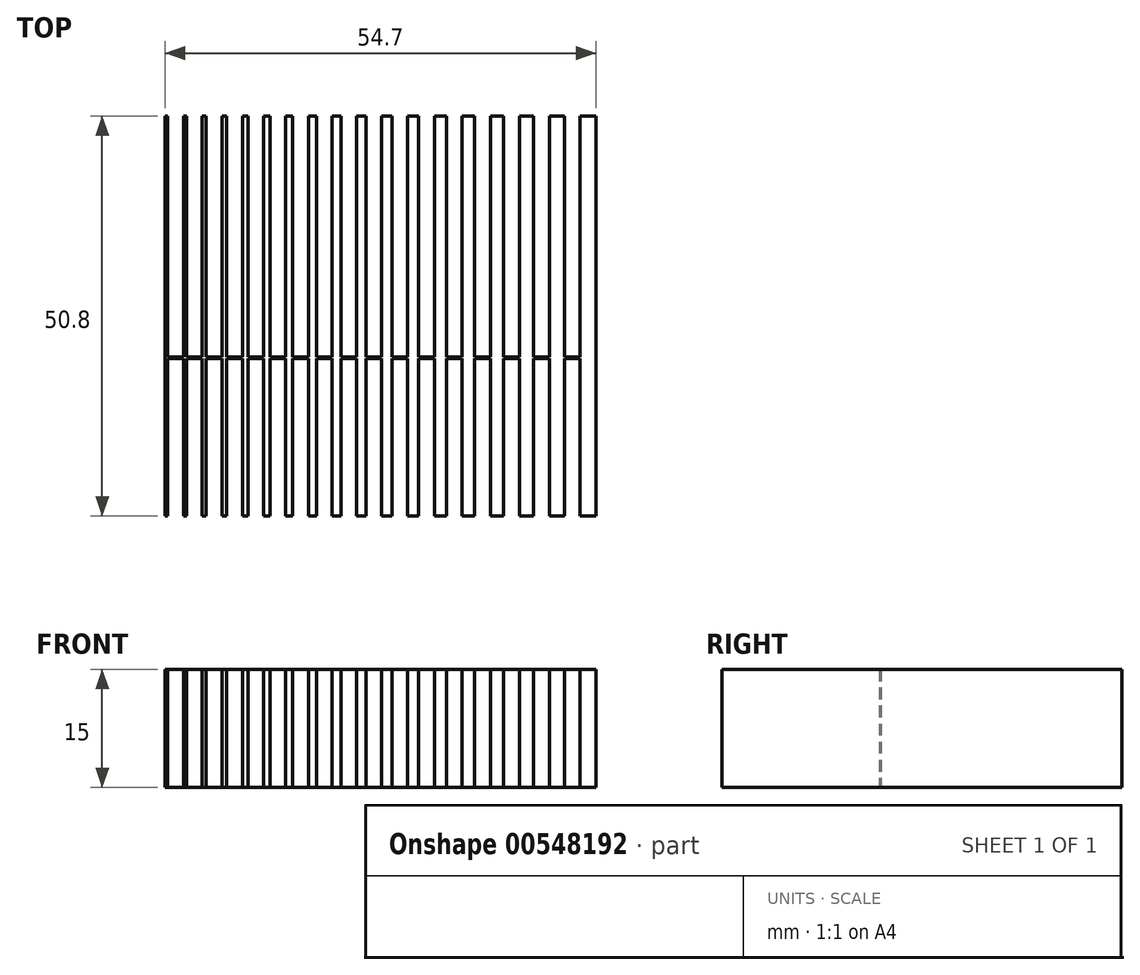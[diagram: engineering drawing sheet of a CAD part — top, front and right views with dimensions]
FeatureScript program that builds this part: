
annotation { "Feature Type Name" : "Feature", "Feature Type Description" : "" }
export const myFeature = defineFeature(function(context is Context, id is Id, definition is map)
    precondition{}
    {
        {
            var Q0;
            Q0=qCreatedBy(makeId("Top.planeOp"),FACE);
            var sketch = newSketch(context, id + "F0", { "sketchPlane" : qUnion([Q0])});
            skLineSegment(sketch, "E0.bottom", {"start": v(-25.4, 25.4) * mm, "end": v(34.6, 25.4) * mm, "construction": true});
            skLineSegment(sketch, "E0.top", {"start": v(-25.4, -25.4) * mm, "end": v(34.6, -25.4) * mm, "construction": true});
            skLineSegment(sketch, "E0.left", {"start": v(-25.4, 25.4) * mm, "end": v(-25.4, -25.4) * mm, "construction": true});
            skLineSegment(sketch, "E0.right", {"start": v(34.6, 25.4) * mm, "end": v(34.6, -25.4) * mm, "construction": true});
            skLineSegment(sketch, "E1.bottom", {"start": v(-23.4, 25.4) * mm, "end": v(-23.1, 25.4) * mm});
            skLineSegment(sketch, "E1.top", {"start": v(-23.4, -25.4) * mm, "end": v(-23.1, -25.4) * mm});
            skLineSegment(sketch, "E1.left", {"start": v(-23.4, 25.4) * mm, "end": v(-23.4, -25.4) * mm});
            skLineSegment(sketch, "E1.right", {"start": v(-23.1, 25.4) * mm, "end": v(-23.1, -5.2) * mm});
            skLineSegment(sketch, "E2.bottom", {"start": v(-21.1, 25.4) * mm, "end": v(-20.7, 25.4) * mm});
            skLineSegment(sketch, "E2.top", {"start": v(-21.1, -25.4) * mm, "end": v(-20.7, -25.4) * mm});
            skLineSegment(sketch, "E2.left", {"start": v(-21.1, 25.4) * mm, "end": v(-21.1, -5.2) * mm});
            skLineSegment(sketch, "E2.right", {"start": v(-20.7, 25.4) * mm, "end": v(-20.7, -5.2) * mm});
            skLineSegment(sketch, "E3.bottom", {"start": v(-18.7, 25.4) * mm, "end": v(-18.2, 25.4) * mm});
            skLineSegment(sketch, "E3.top", {"start": v(-18.7, -25.4) * mm, "end": v(-18.2, -25.4) * mm});
            skLineSegment(sketch, "E3.left", {"start": v(-18.7, 25.4) * mm, "end": v(-18.7, -5.2) * mm});
            skLineSegment(sketch, "E3.right", {"start": v(-18.2, 25.4) * mm, "end": v(-18.2, -5.2) * mm});
            skLineSegment(sketch, "E4.bottom", {"start": v(-16.2, 25.4) * mm, "end": v(-15.6, 25.4) * mm});
            skLineSegment(sketch, "E4.top", {"start": v(-16.2, -25.4) * mm, "end": v(-15.6, -25.4) * mm});
            skLineSegment(sketch, "E4.left", {"start": v(-16.2, 25.4) * mm, "end": v(-16.2, -5.2) * mm});
            skLineSegment(sketch, "E4.right", {"start": v(-15.6, 25.4) * mm, "end": v(-15.6, -5.2) * mm});
            skLineSegment(sketch, "E5.bottom", {"start": v(-13.6, 25.4) * mm, "end": v(-12.9, 25.4) * mm});
            skLineSegment(sketch, "E5.top", {"start": v(-13.6, -25.4) * mm, "end": v(-12.9, -25.4) * mm});
            skLineSegment(sketch, "E5.left", {"start": v(-13.6, 25.4) * mm, "end": v(-13.6, -5.2) * mm});
            skLineSegment(sketch, "E5.right", {"start": v(-12.9, 25.4) * mm, "end": v(-12.9, -5.2) * mm});
            skLineSegment(sketch, "E6.bottom", {"start": v(-10.9, 25.4) * mm, "end": v(-10.1, 25.4) * mm});
            skLineSegment(sketch, "E6.top", {"start": v(-10.9, -25.4) * mm, "end": v(-10.1, -25.4) * mm});
            skLineSegment(sketch, "E6.left", {"start": v(-10.9, 25.4) * mm, "end": v(-10.9, -5.2) * mm});
            skLineSegment(sketch, "E6.right", {"start": v(-10.1, 25.4) * mm, "end": v(-10.1, -5.2) * mm});
            skLineSegment(sketch, "E7.bottom", {"start": v(-8.1, 25.4) * mm, "end": v(-7.2, 25.4) * mm});
            skLineSegment(sketch, "E7.top", {"start": v(-8.1, -25.4) * mm, "end": v(-7.2, -25.4) * mm});
            skLineSegment(sketch, "E7.left", {"start": v(-8.1, 25.4) * mm, "end": v(-8.1, -5.2) * mm});
            skLineSegment(sketch, "E7.right", {"start": v(-7.2, 25.4) * mm, "end": v(-7.2, -5.2) * mm});
            skLineSegment(sketch, "E8.bottom", {"start": v(-5.2, 25.4) * mm, "end": v(-4.2, 25.4) * mm});
            skLineSegment(sketch, "E8.top", {"start": v(-5.2, -25.4) * mm, "end": v(-4.2, -25.4) * mm});
            skLineSegment(sketch, "E8.left", {"start": v(-5.2, 25.4) * mm, "end": v(-5.2, -5.2) * mm});
            skLineSegment(sketch, "E8.right", {"start": v(-4.2, 25.4) * mm, "end": v(-4.2, -5.2) * mm});
            skLineSegment(sketch, "E9.bottom", {"start": v(-2.2, 25.4) * mm, "end": v(-1.1, 25.4) * mm});
            skLineSegment(sketch, "E9.top", {"start": v(-2.2, -25.4) * mm, "end": v(-1.1, -25.4) * mm});
            skLineSegment(sketch, "E9.left", {"start": v(-2.2, 25.4) * mm, "end": v(-2.2, -5.2) * mm});
            skLineSegment(sketch, "E9.right", {"start": v(-1.1, 25.4) * mm, "end": v(-1.1, -5.2) * mm});
            skLineSegment(sketch, "E10.bottom", {"start": v(0.9, 25.4) * mm, "end": v(2.1, 25.4) * mm});
            skLineSegment(sketch, "E10.top", {"start": v(0.9, -25.4) * mm, "end": v(2.1, -25.4) * mm});
            skLineSegment(sketch, "E10.left", {"start": v(0.9, 25.4) * mm, "end": v(0.9, -5.2) * mm});
            skLineSegment(sketch, "E10.right", {"start": v(2.1, 25.4) * mm, "end": v(2.1, -5.2) * mm});
            skLineSegment(sketch, "E11.bottom", {"start": v(4.1, 25.4) * mm, "end": v(5.4, 25.4) * mm});
            skLineSegment(sketch, "E11.top", {"start": v(4.1, -25.4) * mm, "end": v(5.4, -25.4) * mm});
            skLineSegment(sketch, "E11.left", {"start": v(4.1, 25.4) * mm, "end": v(4.1, -5.2) * mm});
            skLineSegment(sketch, "E11.right", {"start": v(5.4, 25.4) * mm, "end": v(5.4, -5.2) * mm});
            skLineSegment(sketch, "E12.bottom", {"start": v(7.4, 25.4) * mm, "end": v(8.8, 25.4) * mm});
            skLineSegment(sketch, "E12.top", {"start": v(7.4, -25.4) * mm, "end": v(8.8, -25.4) * mm});
            skLineSegment(sketch, "E12.left", {"start": v(7.4, 25.4) * mm, "end": v(7.4, -5.2) * mm});
            skLineSegment(sketch, "E12.right", {"start": v(8.8, 25.4) * mm, "end": v(8.8, -5.2) * mm});
            skLineSegment(sketch, "E13.bottom", {"start": v(10.8, 25.4) * mm, "end": v(12.3, 25.4) * mm});
            skLineSegment(sketch, "E13.top", {"start": v(10.8, -25.4) * mm, "end": v(12.3, -25.4) * mm});
            skLineSegment(sketch, "E13.left", {"start": v(10.8, 25.4) * mm, "end": v(10.8, -5.2) * mm});
            skLineSegment(sketch, "E13.right", {"start": v(12.3, 25.4) * mm, "end": v(12.3, -5.2) * mm});
            skLineSegment(sketch, "E14.bottom", {"start": v(14.3, 25.4) * mm, "end": v(15.9, 25.4) * mm});
            skLineSegment(sketch, "E14.top", {"start": v(14.3, -25.4) * mm, "end": v(15.9, -25.4) * mm});
            skLineSegment(sketch, "E14.left", {"start": v(14.3, 25.4) * mm, "end": v(14.3, -5.2) * mm});
            skLineSegment(sketch, "E14.right", {"start": v(15.9, 25.4) * mm, "end": v(15.9, -5.2) * mm});
            skLineSegment(sketch, "E15.bottom", {"start": v(17.9, -25.4) * mm, "end": v(19.6, -25.4) * mm});
            skLineSegment(sketch, "E15.top", {"start": v(17.9, 25.4) * mm, "end": v(19.6, 25.4) * mm});
            skLineSegment(sketch, "E15.left", {"start": v(17.9, -25.4) * mm, "end": v(17.9, -5.4) * mm});
            skLineSegment(sketch, "E15.right", {"start": v(19.6, -25.4) * mm, "end": v(19.6, -5.4) * mm});
            skLineSegment(sketch, "E16.bottom", {"start": v(21.6, 25.4) * mm, "end": v(23.4, 25.4) * mm});
            skLineSegment(sketch, "E16.top", {"start": v(21.6, -25.4) * mm, "end": v(23.4, -25.4) * mm});
            skLineSegment(sketch, "E16.left", {"start": v(21.6, 25.4) * mm, "end": v(21.6, -5.2) * mm});
            skLineSegment(sketch, "E16.right", {"start": v(23.4, 25.4) * mm, "end": v(23.4, -5.2) * mm});
            skLineSegment(sketch, "E17.bottom", {"start": v(25.4, 25.4) * mm, "end": v(27.3, 25.4) * mm});
            skLineSegment(sketch, "E17.top", {"start": v(25.4, -25.4) * mm, "end": v(27.3, -25.4) * mm});
            skLineSegment(sketch, "E17.left", {"start": v(25.4, 25.4) * mm, "end": v(25.4, -5.2) * mm});
            skLineSegment(sketch, "E17.right", {"start": v(27.3, 25.4) * mm, "end": v(27.3, -5.2) * mm});
            skLineSegment(sketch, "E18.bottom", {"start": v(29.3, 25.4) * mm, "end": v(31.3, 25.4) * mm});
            skLineSegment(sketch, "E18.top", {"start": v(29.3, -25.4) * mm, "end": v(31.3, -25.4) * mm});
            skLineSegment(sketch, "E18.left", {"start": v(29.3, 25.4) * mm, "end": v(29.3, -5.2) * mm});
            skLineSegment(sketch, "E18.right", {"start": v(31.3, 25.4) * mm, "end": v(31.3, -25.4) * mm});
            skLineSegment(sketch, "E19.bottom", {"start": v(-23.1, -5.2) * mm, "end": v(-21.1, -5.2) * mm});
            skLineSegment(sketch, "E19.top", {"start": v(-23.1, -5.4) * mm, "end": v(-21.1, -5.4) * mm});
            skLineSegment(sketch, "E19.right", {"start": v(31.3, -5.2) * mm, "end": v(31.3, -5.4) * mm});
            skLineSegment(sketch, "E20.trimOffspring", {"start": v(29.3, -5.4) * mm, "end": v(29.3, -25.4) * mm});
            skLineSegment(sketch, "E21.trimOffspring", {"start": v(27.3, -5.4) * mm, "end": v(27.3, -25.4) * mm});
            skLineSegment(sketch, "E22.trimOffspring", {"start": v(27.3, -5.2) * mm, "end": v(29.3, -5.2) * mm});
            skLineSegment(sketch, "E23.trimOffspring", {"start": v(27.3, -5.4) * mm, "end": v(29.3, -5.4) * mm});
            skLineSegment(sketch, "E24.trimOffspring", {"start": v(25.4, -5.4) * mm, "end": v(25.4, -25.4) * mm});
            skLineSegment(sketch, "E25.trimOffspring", {"start": v(23.4, -5.4) * mm, "end": v(23.4, -25.4) * mm});
            skLineSegment(sketch, "E26.trimOffspring", {"start": v(23.4, -5.2) * mm, "end": v(25.4, -5.2) * mm});
            skLineSegment(sketch, "E27.trimOffspring", {"start": v(23.4, -5.4) * mm, "end": v(25.4, -5.4) * mm});
            skLineSegment(sketch, "E28.trimOffspring", {"start": v(21.6, -5.4) * mm, "end": v(21.6, -25.4) * mm});
            skLineSegment(sketch, "E29.trimOffspring", {"start": v(19.6, -5.2) * mm, "end": v(19.6, 25.4) * mm});
            skLineSegment(sketch, "E30.trimOffspring", {"start": v(19.6, -5.2) * mm, "end": v(21.6, -5.2) * mm});
            skLineSegment(sketch, "E31.trimOffspring", {"start": v(19.6, -5.4) * mm, "end": v(21.6, -5.4) * mm});
            skLineSegment(sketch, "E32.trimOffspring", {"start": v(17.9, -5.2) * mm, "end": v(17.9, 25.4) * mm});
            skLineSegment(sketch, "E33.trimOffspring", {"start": v(15.9, -5.4) * mm, "end": v(15.9, -25.4) * mm});
            skLineSegment(sketch, "E34.trimOffspring", {"start": v(15.9, -5.2) * mm, "end": v(17.9, -5.2) * mm});
            skLineSegment(sketch, "E35.trimOffspring", {"start": v(15.9, -5.4) * mm, "end": v(17.9, -5.4) * mm});
            skLineSegment(sketch, "E36.trimOffspring", {"start": v(14.3, -5.4) * mm, "end": v(14.3, -25.4) * mm});
            skLineSegment(sketch, "E37.trimOffspring", {"start": v(12.3, -5.4) * mm, "end": v(12.3, -25.4) * mm});
            skLineSegment(sketch, "E38.trimOffspring", {"start": v(12.3, -5.2) * mm, "end": v(14.3, -5.2) * mm});
            skLineSegment(sketch, "E39.trimOffspring", {"start": v(12.3, -5.4) * mm, "end": v(14.3, -5.4) * mm});
            skLineSegment(sketch, "E40.trimOffspring", {"start": v(10.8, -5.4) * mm, "end": v(10.8, -25.4) * mm});
            skLineSegment(sketch, "E41.trimOffspring", {"start": v(8.8, -5.4) * mm, "end": v(8.8, -25.4) * mm});
            skLineSegment(sketch, "E42.trimOffspring", {"start": v(8.8, -5.2) * mm, "end": v(10.8, -5.2) * mm});
            skLineSegment(sketch, "E43.trimOffspring", {"start": v(7.4, -5.4) * mm, "end": v(7.4, -25.4) * mm});
            skLineSegment(sketch, "E44.trimOffspring", {"start": v(8.8, -5.4) * mm, "end": v(10.8, -5.4) * mm});
            skLineSegment(sketch, "E45.trimOffspring", {"start": v(5.4, -5.4) * mm, "end": v(5.4, -25.4) * mm});
            skLineSegment(sketch, "E46.trimOffspring", {"start": v(5.4, -5.2) * mm, "end": v(7.4, -5.2) * mm});
            skLineSegment(sketch, "E47.trimOffspring", {"start": v(4.1, -5.4) * mm, "end": v(4.1, -25.4) * mm});
            skLineSegment(sketch, "E48.trimOffspring", {"start": v(5.4, -5.4) * mm, "end": v(7.4, -5.4) * mm});
            skLineSegment(sketch, "E49.trimOffspring", {"start": v(2.1, -5.4) * mm, "end": v(2.1, -25.4) * mm});
            skLineSegment(sketch, "E50.trimOffspring", {"start": v(2.1, -5.2) * mm, "end": v(4.1, -5.2) * mm});
            skLineSegment(sketch, "E51.trimOffspring", {"start": v(2.1, -5.4) * mm, "end": v(4.1, -5.4) * mm});
            skLineSegment(sketch, "E52.trimOffspring", {"start": v(0.9, -5.4) * mm, "end": v(0.9, -25.4) * mm});
            skLineSegment(sketch, "E53.trimOffspring", {"start": v(-1.1, -5.4) * mm, "end": v(-1.1, -25.4) * mm});
            skLineSegment(sketch, "E54.trimOffspring", {"start": v(-1.1, -5.2) * mm, "end": v(0.9, -5.2) * mm});
            skLineSegment(sketch, "E55.trimOffspring", {"start": v(-1.1, -5.4) * mm, "end": v(0.9, -5.4) * mm});
            skLineSegment(sketch, "E56.trimOffspring", {"start": v(-2.2, -5.4) * mm, "end": v(-2.2, -25.4) * mm});
            skLineSegment(sketch, "E57.trimOffspring", {"start": v(-4.2, -5.4) * mm, "end": v(-4.2, -25.4) * mm});
            skLineSegment(sketch, "E58.trimOffspring", {"start": v(-4.2, -5.2) * mm, "end": v(-2.2, -5.2) * mm});
            skLineSegment(sketch, "E59.trimOffspring", {"start": v(-5.2, -5.4) * mm, "end": v(-5.2, -25.4) * mm});
            skLineSegment(sketch, "E60.trimOffspring", {"start": v(-4.2, -5.4) * mm, "end": v(-2.2, -5.4) * mm});
            skLineSegment(sketch, "E61.trimOffspring", {"start": v(-7.2, -5.4) * mm, "end": v(-7.2, -25.4) * mm});
            skLineSegment(sketch, "E62.trimOffspring", {"start": v(-7.2, -5.2) * mm, "end": v(-5.2, -5.2) * mm});
            skLineSegment(sketch, "E63.trimOffspring", {"start": v(-8.1, -5.4) * mm, "end": v(-8.1, -25.4) * mm});
            skLineSegment(sketch, "E64.trimOffspring", {"start": v(-7.2, -5.4) * mm, "end": v(-5.2, -5.4) * mm});
            skLineSegment(sketch, "E65.trimOffspring", {"start": v(-10.1, -5.4) * mm, "end": v(-10.1, -25.4) * mm});
            skLineSegment(sketch, "E66.trimOffspring", {"start": v(-10.9, -5.4) * mm, "end": v(-10.9, -25.4) * mm});
            skLineSegment(sketch, "E67.trimOffspring", {"start": v(-10.1, -5.2) * mm, "end": v(-8.1, -5.2) * mm});
            skLineSegment(sketch, "E68.trimOffspring", {"start": v(-10.1, -5.4) * mm, "end": v(-8.1, -5.4) * mm});
            skLineSegment(sketch, "E69.trimOffspring", {"start": v(-12.9, -5.4) * mm, "end": v(-10.9, -5.4) * mm});
            skLineSegment(sketch, "E70.trimOffspring", {"start": v(-12.9, -5.4) * mm, "end": v(-12.9, -25.4) * mm});
            skLineSegment(sketch, "E71.trimOffspring", {"start": v(-12.9, -5.2) * mm, "end": v(-10.9, -5.2) * mm});
            skLineSegment(sketch, "E72.trimOffspring", {"start": v(-13.6, -5.4) * mm, "end": v(-13.6, -25.4) * mm});
            skLineSegment(sketch, "E73.trimOffspring", {"start": v(-15.6, -5.2) * mm, "end": v(-13.6, -5.2) * mm});
            skLineSegment(sketch, "E74.trimOffspring", {"start": v(-16.2, -5.4) * mm, "end": v(-16.2, -25.4) * mm});
            skLineSegment(sketch, "E75.trimOffspring", {"start": v(-15.6, -5.4) * mm, "end": v(-13.6, -5.4) * mm});
            skLineSegment(sketch, "E76.trimOffspring", {"start": v(-15.6, -5.4) * mm, "end": v(-15.6, -25.4) * mm});
            skLineSegment(sketch, "E77.trimOffspring", {"start": v(-18.2, -5.4) * mm, "end": v(-18.2, -25.4) * mm});
            skLineSegment(sketch, "E78.trimOffspring", {"start": v(-18.2, -5.2) * mm, "end": v(-16.2, -5.2) * mm});
            skLineSegment(sketch, "E79.trimOffspring", {"start": v(-18.7, -5.4) * mm, "end": v(-18.7, -25.4) * mm});
            skLineSegment(sketch, "E80.trimOffspring", {"start": v(-18.2, -5.4) * mm, "end": v(-16.2, -5.4) * mm});
            skLineSegment(sketch, "E81.trimOffspring", {"start": v(-20.7, -5.4) * mm, "end": v(-20.7, -25.4) * mm});
            skLineSegment(sketch, "E82.trimOffspring", {"start": v(-20.7, -5.2) * mm, "end": v(-18.7, -5.2) * mm});
            skLineSegment(sketch, "E83.trimOffspring", {"start": v(-21.1, -5.4) * mm, "end": v(-21.1, -25.4) * mm});
            skLineSegment(sketch, "E84.trimOffspring", {"start": v(-20.7, -5.4) * mm, "end": v(-18.7, -5.4) * mm});
            skLineSegment(sketch, "E85.trimOffspring", {"start": v(-23.1, -5.4) * mm, "end": v(-23.1, -25.4) * mm});
            skSolve(sketch);
        }
        {
            var Q0;
            Q0=makeQuery(id+"F0.imprint","IMPRINT",FACE,{"disambiguationData":[TD([[makeQuery(id+"F0.imprint","IMPRINT",EDGE,{"derivedFrom":sQuery(id+"F0.wireOp",EDGE,"E1.bottom")}),-1.0]])]});
            extrude(context, id + "F1", {"entities" : qUnion([Q0]), "depth" : 15 * mm, "offsetDistance" : 25 * mm});
        }
    });
